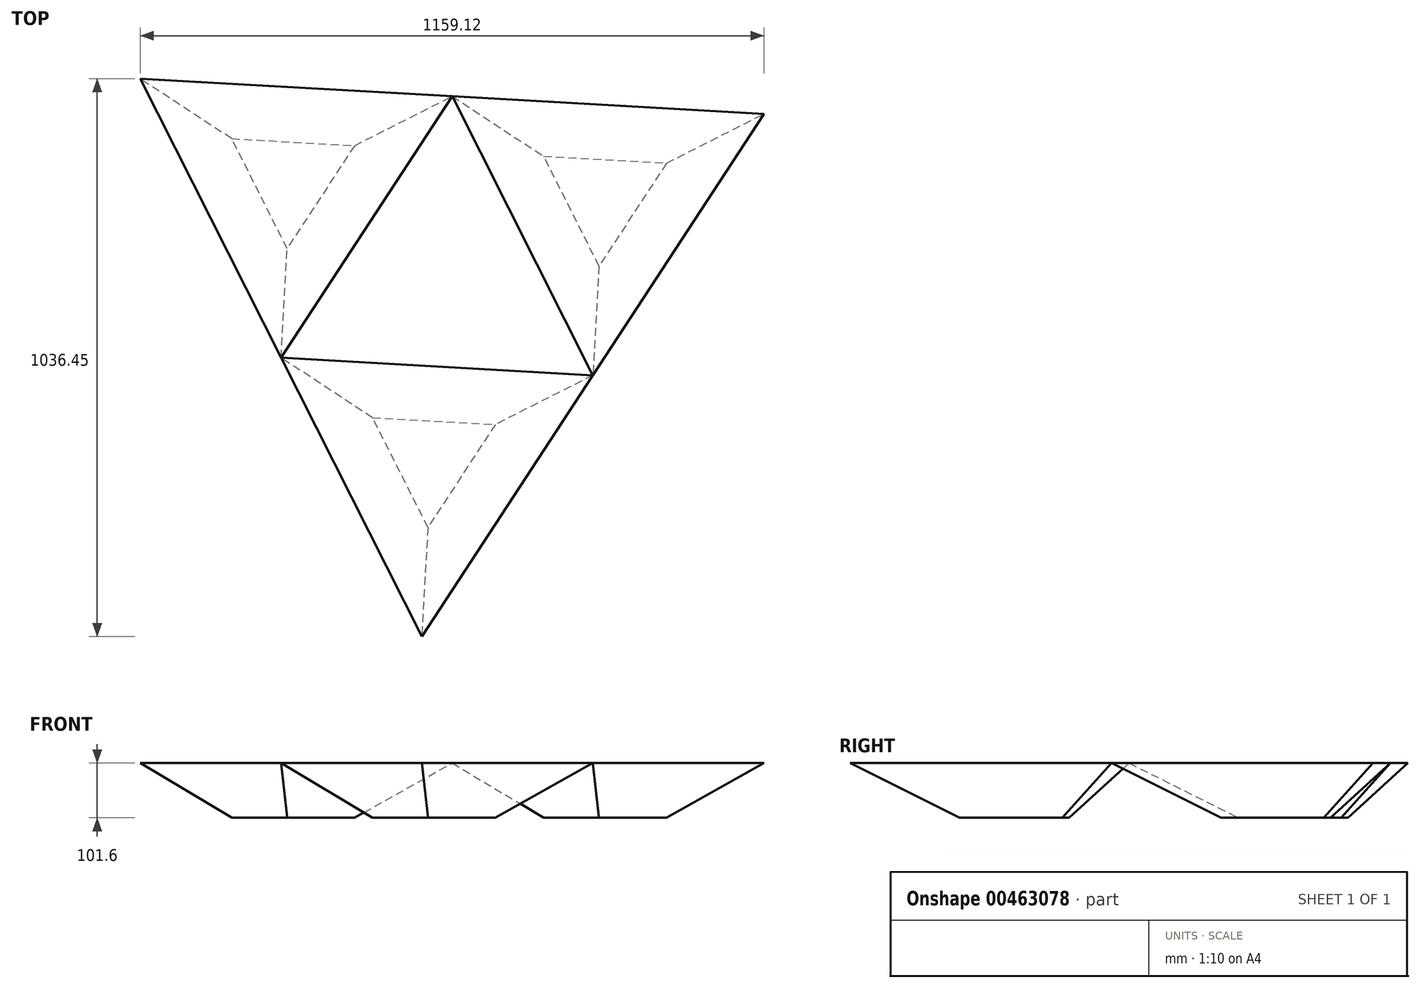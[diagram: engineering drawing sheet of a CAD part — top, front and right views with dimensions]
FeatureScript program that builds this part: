
annotation { "Feature Type Name" : "Feature", "Feature Type Description" : "" }
export const myFeature = defineFeature(function(context is Context, id is Id, definition is map)
    precondition{}
    {
        {
            var Q0;
            Q0=qCreatedBy(makeId("Top.planeOp"),FACE);
            var sketch = newSketch(context, id + "F0", { "sketchPlane" : qUnion([Q0])});
            skCircle(sketch, "E0.cCircle", {"center": v(0, 0) * mm, "radius": 670.28 * mm, "construction": true});
            skLineSegment(sketch, "E0.0", {"start": v(598.4, 302) * mm, "end": v(-37.66, -669.22) * mm});
            skLineSegment(sketch, "E0.1", {"start": v(-37.66, -669.22) * mm, "end": v(-560.73, 367.23) * mm});
            skLineSegment(sketch, "E0.2", {"start": v(-560.73, 367.23) * mm, "end": v(598.4, 302) * mm});
            skCircle(sketch, "E1.cCircle", {"center": v(0, 0) * mm, "radius": 335.14 * mm, "construction": true});
            skLineSegment(sketch, "E1.0", {"start": v(280.37, -183.61) * mm, "end": v(-299.2, -151) * mm});
            skLineSegment(sketch, "E1.1", {"start": v(-299.2, -151) * mm, "end": v(18.83, 334.61) * mm});
            skLineSegment(sketch, "E1.2", {"start": v(18.83, 334.61) * mm, "end": v(280.37, -183.61) * mm});
            skSolve(sketch);
        }
        {
            var Q0;
            {var subQ3=sQuery(id+"F0.wireOp",EDGE,"E1.2");Q0=makeQuery(id+"F0.imprint","IMPRINT",FACE,{"disambiguationData":[TD([[makeQuery(id+"F0.imprint","IMPRINT",EDGE,{"derivedFrom":subQ3}),1.0]])]});}
            var Q1;
            {var subQ3=sQuery(id+"F0.wireOp",EDGE,"E1.0");Q1=makeQuery(id+"F0.imprint","IMPRINT",FACE,{"disambiguationData":[TD([[makeQuery(id+"F0.imprint","IMPRINT",EDGE,{"derivedFrom":subQ3}),1.0]])]});}
            var Q2;
            {var subQ3=sQuery(id+"F0.wireOp",EDGE,"E1.1");Q2=makeQuery(id+"F0.imprint","IMPRINT",FACE,{"disambiguationData":[TD([[makeQuery(id+"F0.imprint","IMPRINT",EDGE,{"derivedFrom":subQ3}),1.0]])]});}
            extrude(context, id + "F1", {"entities" : qUnion([Q0, Q1, Q2]), "endBound" : BoundingType.SYMMETRIC, "depth" : 101.6 * mm});
        }
        {
            var Q0;
            {var subQ0=sQuery(id+"F0.wireOp",EDGE,"E0.2");Q0=makeQuery(id+"F1.opExtrude","CAP_EDGE",EDGE,{"disambiguationData":[OSD([subQ0]),TDD([makeQuery(id+"F0.imprint","IMPRINT",EDGE,{"disambiguationData":[TD([[makeQuery(id+"F0.imprint","INTERSECT",VERTEX,{"derivedFrom":[sQuery(id+"F0.wireOp",EDGE,"E0.0"),subQ0]}),1.0]])],"derivedFrom":subQ0})])],"isStart":true});}
            var Q1;
            {var subQ0=sQuery(id+"F0.wireOp",EDGE,"E0.0");Q1=makeQuery(id+"F1.opExtrude","CAP_EDGE",EDGE,{"disambiguationData":[OSD([subQ0]),TDD([makeQuery(id+"F0.imprint","IMPRINT",EDGE,{"disambiguationData":[TD([[makeQuery(id+"F0.imprint","INTERSECT",VERTEX,{"derivedFrom":[subQ0,sQuery(id+"F0.wireOp",EDGE,"E0.2")]}),-1.0]])],"derivedFrom":subQ0})])],"isStart":true});}
            var Q2;
            Q2=makeQuery(id+"F1.opExtrude","CAP_EDGE",EDGE,{"disambiguationData":[OSD([sQuery(id+"F0.wireOp",EDGE,"E1.2")])],"isStart":true});
            var Q3;
            Q3=makeQuery(id+"F1.opExtrude","CAP_EDGE",EDGE,{"disambiguationData":[OSD([sQuery(id+"F0.wireOp",EDGE,"E1.0")])],"isStart":true});
            var Q4;
            {var subQ0=sQuery(id+"F0.wireOp",EDGE,"E0.0");Q4=makeQuery(id+"F1.opExtrude","CAP_EDGE",EDGE,{"disambiguationData":[OSD([subQ0]),TDD([makeQuery(id+"F0.imprint","IMPRINT",EDGE,{"disambiguationData":[TD([[makeQuery(id+"F0.imprint","INTERSECT",VERTEX,{"derivedFrom":[subQ0,sQuery(id+"F0.wireOp",EDGE,"E0.1")]}),1.0]])],"derivedFrom":subQ0})])],"isStart":true});}
            var Q5;
            {var subQ0=sQuery(id+"F0.wireOp",EDGE,"E0.1");Q5=makeQuery(id+"F1.opExtrude","CAP_EDGE",EDGE,{"disambiguationData":[OSD([subQ0]),TDD([makeQuery(id+"F0.imprint","IMPRINT",EDGE,{"disambiguationData":[TD([[makeQuery(id+"F0.imprint","INTERSECT",VERTEX,{"derivedFrom":[sQuery(id+"F0.wireOp",EDGE,"E0.0"),subQ0]}),-1.0]])],"derivedFrom":subQ0})])],"isStart":true});}
            var Q6;
            {var subQ0=sQuery(id+"F0.wireOp",EDGE,"E0.1");Q6=makeQuery(id+"F1.opExtrude","CAP_EDGE",EDGE,{"disambiguationData":[OSD([subQ0]),TDD([makeQuery(id+"F0.imprint","IMPRINT",EDGE,{"disambiguationData":[TD([[makeQuery(id+"F0.imprint","INTERSECT",VERTEX,{"derivedFrom":[subQ0,sQuery(id+"F0.wireOp",EDGE,"E0.2")]}),1.0]])],"derivedFrom":subQ0})])],"isStart":true});}
            var Q7;
            {var subQ0=sQuery(id+"F0.wireOp",EDGE,"E0.2");Q7=makeQuery(id+"F1.opExtrude","CAP_EDGE",EDGE,{"disambiguationData":[OSD([subQ0]),TDD([makeQuery(id+"F0.imprint","IMPRINT",EDGE,{"disambiguationData":[TD([[makeQuery(id+"F0.imprint","INTERSECT",VERTEX,{"derivedFrom":[sQuery(id+"F0.wireOp",EDGE,"E0.1"),subQ0]}),-1.0]])],"derivedFrom":subQ0})])],"isStart":true});}
            var Q8;
            Q8=makeQuery(id+"F1.opExtrude","CAP_EDGE",EDGE,{"disambiguationData":[OSD([sQuery(id+"F0.wireOp",EDGE,"E1.1")])],"isStart":true});
            chamfer(context, id + "F2", {"entities" : qUnion([Q0, Q1, Q2, Q3, Q4, Q5, Q6, Q7, Q8]), "width" : 101.6 * mm, "tangentPropagation" : true});
        }
    });
